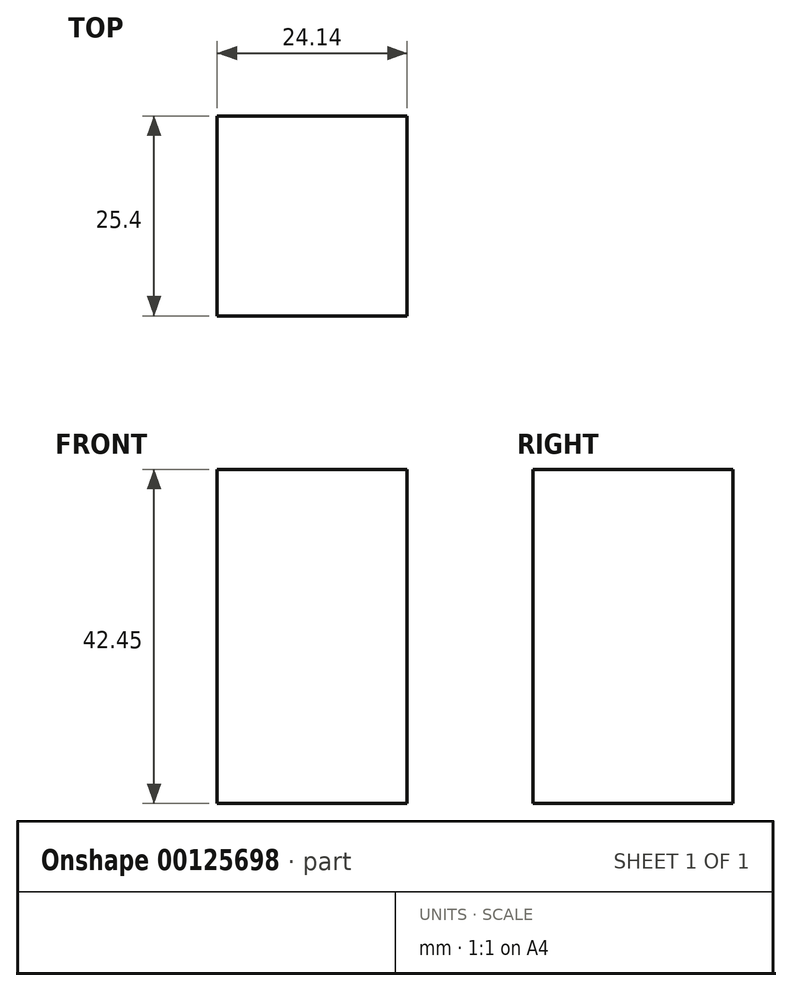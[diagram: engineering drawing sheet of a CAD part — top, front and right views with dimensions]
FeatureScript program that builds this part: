
annotation { "Feature Type Name" : "Feature", "Feature Type Description" : "" }
export const myFeature = defineFeature(function(context is Context, id is Id, definition is map)
    precondition{}
    {
        {
            var Q0;
            Q0=qCreatedBy(makeId("Front.planeOp"),FACE);
            var sketch = newSketch(context, id + "F0", { "sketchPlane" : qUnion([Q0])});
            skLineSegment(sketch, "E0", {"start": v(-53.2, 29.26) * mm, "end": v(26.28, 67.46) * mm});
            skLineSegment(sketch, "E1.bottom", {"start": v(8.74, 26.88) * mm, "end": v(32.88, 26.88) * mm});
            skLineSegment(sketch, "E1.top", {"start": v(8.74, -15.57) * mm, "end": v(32.88, -15.57) * mm});
            skLineSegment(sketch, "E1.left", {"start": v(8.74, 26.88) * mm, "end": v(8.74, -15.57) * mm});
            skLineSegment(sketch, "E1.right", {"start": v(32.88, 26.88) * mm, "end": v(32.88, -15.57) * mm});
            skSolve(sketch);
        }
        {
            var Q0;
            Q0 = qSketchRegion(id + "F0", true);
            extrude(context, id + "F1", {"entities" : qUnion([Q0]), "depth" : 25.4 * mm});
        }
    });
